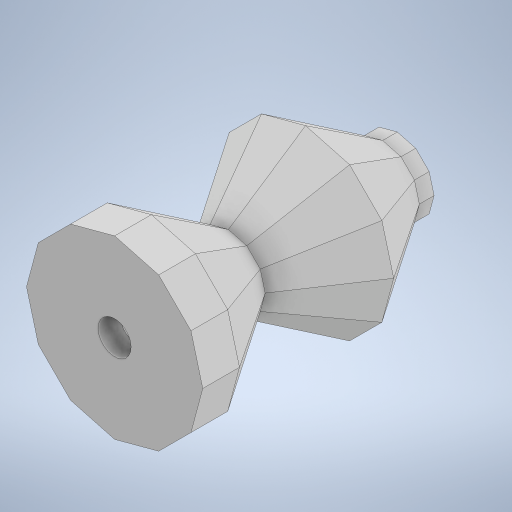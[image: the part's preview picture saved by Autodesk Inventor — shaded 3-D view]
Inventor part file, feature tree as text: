
AUTODESK INVENTOR PART (.ipt)
format: ipt  version: 2023 (Build 270158000, 158)  size: 353,280 bytes
history: native  units: in
note: dims shown in document units (in); Inventor stores cm internally (conversion verified against a paired STEP export)
features: sketch x6, extrude x4, projected_geometry x3, other x2, mirror x2, loft x1, shell x1
ambient origin geometry x8: Origin, YZ Plane, XZ Plane, XY Plane, X Axis, Y Axis, Z Axis, Center Point
bodies: Body1 (feature_tree)
feature tree (19):
  other  "솔리드1"
  sketch  "스케치1"
  other  "작업 평면1"
  loft  "로프트1"
  mirror  "미러1"
  mirror  "미러2"
  extrude  "돌출5"  Depth=0.4134in
  shell  "쉘2"  Thickness=0.3937in
  extrude  "돌출6"  TaperAngle=0.0deg  [1 undecoded]
  extrude  "돌출7"  TaperAngle=0.0deg  [1 undecoded]
  extrude  "돌출8"  Depth=0.0984in TaperAngle=0.0deg
  sketch  "스케치2"
  sketch  "스케치7"
  projected_geometry  "투영된 루프4"
  sketch  "스케치8"
  projected_geometry  "투영된 루프5"
  sketch  "스케치9"
  sketch  "스케치10"
  projected_geometry  "투영된 루프6"
note: 2 required parameter values undecoded (feature->parameter linkage not recoverable at this tier; creation-order binding heuristic only, values carry confidence <= 0.55)
